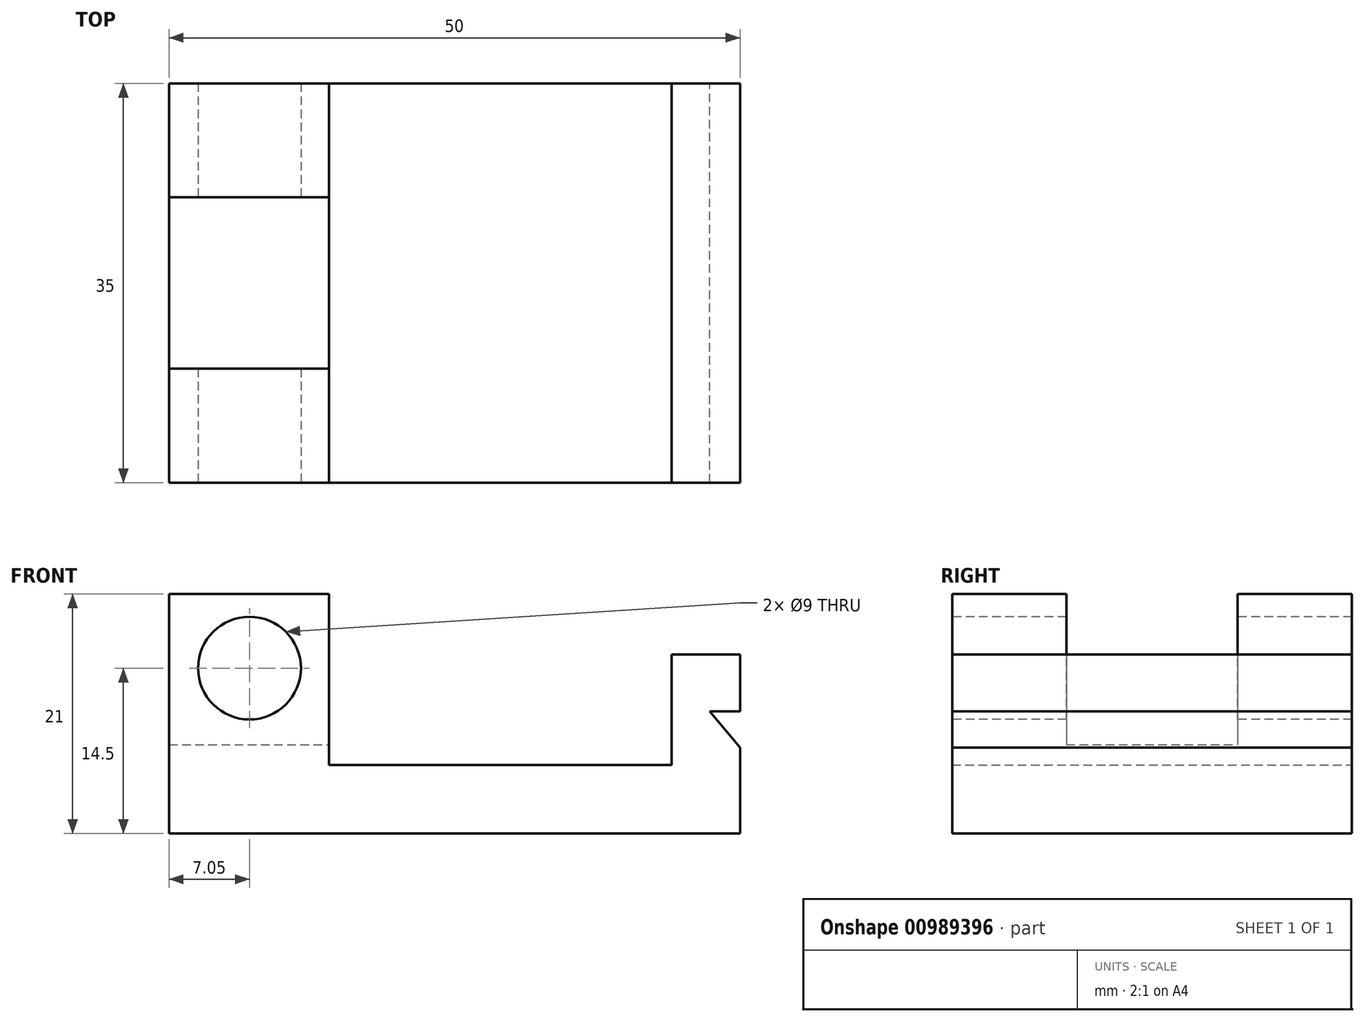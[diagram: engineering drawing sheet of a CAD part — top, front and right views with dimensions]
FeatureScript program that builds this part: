
annotation { "Feature Type Name" : "Feature", "Feature Type Description" : "" }
export const myFeature = defineFeature(function(context is Context, id is Id, definition is map)
    precondition{}
    {
        {
            var Q0;
            Q0=qCreatedBy(makeId("Top.planeOp"),FACE);
            var sketch = newSketch(context, id + "F0", { "sketchPlane" : qUnion([Q0])});
            skLineSegment(sketch, "E0.bottom", {"start": v(-25, 17.5) * mm, "end": v(25, 17.5) * mm});
            skLineSegment(sketch, "E0.top", {"start": v(-25, -17.5) * mm, "end": v(25, -17.5) * mm});
            skLineSegment(sketch, "E0.left", {"start": v(-25, 17.5) * mm, "end": v(-25, -17.5) * mm});
            skLineSegment(sketch, "E0.right", {"start": v(25, 17.5) * mm, "end": v(25, -17.5) * mm});
            skPoint(sketch, "E0.middle", {"position": v(0, 0) * mm});
            skSolve(sketch);
        }
        {
            var Q0;
            Q0=makeQuery(id+"F0.imprint","IMPRINT",FACE,{"disambiguationData":[TD([[makeQuery(id+"F0.imprint","IMPRINT",EDGE,{"derivedFrom":sQuery(id+"F0.wireOp",EDGE,"E0.bottom")}),-1.0]])]});
            extrude(context, id + "F1", {"entities" : qUnion([Q0]), "depth" : 6 * mm, "offsetDistance" : 25 * mm});
        }
        {
            var Q0;
            Q0=makeQuery(id+"F1.opExtrude","CAP_FACE",FACE,{"disambiguationData":[OSD([sQuery(id+"F0.wireOp",EDGE,"E0.bottom"),sQuery(id+"F0.wireOp",EDGE,"E0.top"),sQuery(id+"F0.wireOp",EDGE,"E0.left"),sQuery(id+"F0.wireOp",EDGE,"E0.right")])],"isStart":false});
            var sketch = newSketch(context, id + "F2", { "sketchPlane" : qUnion([Q0])});
            skLineSegment(sketch, "E1.bottom", {"start": v(-25, -17.5) * mm, "end": v(-11, -17.5) * mm});
            skLineSegment(sketch, "E1.top", {"start": v(-25, 17.5) * mm, "end": v(-11, 17.5) * mm});
            skLineSegment(sketch, "E1.left", {"start": v(-25, -17.5) * mm, "end": v(-25, 17.5) * mm});
            skLineSegment(sketch, "E1.right", {"start": v(-11, -17.5) * mm, "end": v(-11, 17.5) * mm});
            skSolve(sketch);
        }
        {
            var Q0;
            Q0=makeQuery(id+"F2.imprint","IMPRINT",FACE,{"disambiguationData":[TD([[makeQuery(id+"F2.imprint","IMPRINT",EDGE,{"derivedFrom":sQuery(id+"F2.wireOp",EDGE,"E1.bottom")}),1.0]])]});
            extrude(context, id + "F3", {"entities" : qUnion([Q0]), "operationType" : NewBodyOperationType.ADD, "depth" : 15 * mm, "offsetDistance" : 25 * mm});
        }
        {
            var Q0;
            Q0=makeQuery(id+"F3.opExtrude","SWEPT_FACE",FACE,{"disambiguationData":[OSD([sQuery(id+"F2.wireOp",EDGE,"E1.right")])]});
            var sketch = newSketch(context, id + "F4", { "sketchPlane" : qUnion([Q0])});
            skLineSegment(sketch, "E2.bottom", {"start": v(-7.5, 21) * mm, "end": v(7.5, 21) * mm});
            skLineSegment(sketch, "E2.top", {"start": v(-7.5, 7.78) * mm, "end": v(7.5, 7.78) * mm});
            skLineSegment(sketch, "E2.left", {"start": v(-7.5, 21) * mm, "end": v(-7.5, 7.78) * mm});
            skLineSegment(sketch, "E2.right", {"start": v(7.5, 21) * mm, "end": v(7.5, 7.78) * mm});
            skSolve(sketch);
        }
        {
            var Q0;
            Q0=makeQuery(id+"F4.imprint","IMPRINT",FACE,{"disambiguationData":[TD([[makeQuery(id+"F4.imprint","IMPRINT",EDGE,{"derivedFrom":sQuery(id+"F4.wireOp",EDGE,"E2.bottom")}),-1.0]])]});
            extrude(context, id + "F5", {"entities" : qUnion([Q0]), "operationType" : NewBodyOperationType.REMOVE, "oppositeDirection" : true, "depth" : 25 * mm, "offsetDistance" : 25 * mm});
        }
        {
            var Q0;
            Q0=makeQuery(id+"F3.boolean.opBoolean","MERGE",FACE,{"derivedFrom":[makeQuery(id+"F1.opExtrude","SWEPT_FACE",FACE,{"disambiguationData":[OSD([sQuery(id+"F0.wireOp",EDGE,"E0.top")])]}),makeQuery(id+"F3.opExtrude","SWEPT_FACE",FACE,{"disambiguationData":[OSD([sQuery(id+"F2.wireOp",EDGE,"E1.bottom")])]})]});
            var sketch = newSketch(context, id + "F6", { "sketchPlane" : qUnion([Q0])});
            skCircle(sketch, "E3", {"center": v(-17.95, 14.5) * mm, "radius": 4.5 * mm});
            skSolve(sketch);
        }
        {
            var Q0;
            Q0=makeQuery(id+"F6.imprint","IMPRINT",FACE,{"disambiguationData":[TD([[makeQuery(id+"F6.imprint","IMPRINT",EDGE,{"derivedFrom":sQuery(id+"F6.wireOp",EDGE,"E3")}),1.0]])]});
            extrude(context, id + "F7", {"entities" : qUnion([Q0]), "operationType" : NewBodyOperationType.REMOVE, "oppositeDirection" : true, "depth" : 41.5 * mm, "offsetDistance" : 25 * mm});
        }
        {
            var Q0;
            Q0=makeQuery(id+"F1.opExtrude","CAP_FACE",FACE,{"disambiguationData":[OSD([sQuery(id+"F0.wireOp",EDGE,"E0.bottom"),sQuery(id+"F0.wireOp",EDGE,"E0.top"),sQuery(id+"F0.wireOp",EDGE,"E0.left"),sQuery(id+"F0.wireOp",EDGE,"E0.right")])],"isStart":false});
            var sketch = newSketch(context, id + "F8", { "sketchPlane" : qUnion([Q0])});
            skLineSegment(sketch, "E4.bottom", {"start": v(25, 17.5) * mm, "end": v(19, 17.5) * mm});
            skLineSegment(sketch, "E4.top", {"start": v(25, -17.5) * mm, "end": v(19, -17.5) * mm});
            skLineSegment(sketch, "E4.left", {"start": v(25, 17.5) * mm, "end": v(25, -17.5) * mm});
            skLineSegment(sketch, "E4.right", {"start": v(19, 17.5) * mm, "end": v(19, -17.5) * mm});
            skSolve(sketch);
        }
        {
            var Q0;
            Q0 = qSketchRegion(id + "F8", true);
            extrude(context, id + "F9", {"entities" : qUnion([Q0]), "operationType" : NewBodyOperationType.ADD, "depth" : 9.7 * mm, "offsetDistance" : 25 * mm});
        }
        {
            var Q0;
            Q0=makeQuery(id+"F9.boolean.opBoolean","MERGE",FACE,{"derivedFrom":[makeQuery(id+"F3.boolean.opBoolean","MERGE",FACE,{"derivedFrom":[makeQuery(id+"F1.opExtrude","SWEPT_FACE",FACE,{"disambiguationData":[OSD([sQuery(id+"F0.wireOp",EDGE,"E0.bottom")])]}),makeQuery(id+"F3.opExtrude","SWEPT_FACE",FACE,{"disambiguationData":[OSD([sQuery(id+"F2.wireOp",EDGE,"E1.top")])]})]}),makeQuery(id+"F9.opExtrude","SWEPT_FACE",FACE,{"disambiguationData":[OSD([sQuery(id+"F8.wireOp",EDGE,"E4.bottom")])]})]});
            var sketch = newSketch(context, id + "F10", { "sketchPlane" : qUnion([Q0])});
            skLineSegment(sketch, "E5", {"start": v(-25, 10.7) * mm, "end": v(-22.36, 10.7) * mm});
            skLineSegment(sketch, "E6", {"start": v(-22.36, 10.7) * mm, "end": v(-25, 7.55) * mm});
            skLineSegment(sketch, "E7", {"start": v(-25, 7.55) * mm, "end": v(-25, 10.7) * mm});
            skSolve(sketch);
        }
        {
            var Q0;
            Q0 = qSketchRegion(id + "F10", true);
            extrude(context, id + "F11", {"entities" : qUnion([Q0]), "operationType" : NewBodyOperationType.REMOVE, "oppositeDirection" : true, "depth" : 36.8 * mm, "offsetDistance" : 25 * mm});
        }
    });
